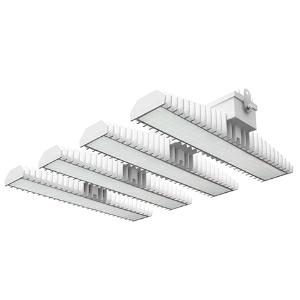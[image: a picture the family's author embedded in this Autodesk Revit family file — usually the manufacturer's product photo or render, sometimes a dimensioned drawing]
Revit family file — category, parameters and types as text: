
# Revit family: 3f_filippi_-_3f_lem_ht_concentrato_3f_filippi_-_59034_a0812_-_3f_lem_4_ht_led_120_cr_conc___vs_332a
name_source: partatom
category: Lighting Fixtures
units: mm (PartAtom-declared; Revit-internal decimal feet)

## family parameters
Cut with Voids When Loaded = No
Host = Face
Light Source = No
Part Type = Normal
Room Calculation Point = No
Round Connector Dimension = Use Diameter
Shared = No

## types (1)
- 3F Filippi - 3F LEM HT Concentrato (1 x LED, 16911 lm, 136 W, 4000 K)
    Apparent Load = 136 VA
    Approval mark = ENEC
    CIE Flux Codes = 78 93 98 100 100
    Color Rendering = 80
    Color Temperature = 4000 K
    Control Gear = Electronic ballast
    Default Elevation = 1800 mm
    Description = Industrial luminaire with high light output and high luminous efficiency designed with the most innovative technologies for environments with temperature up to 70°C.

ILLUMINOTECHNICAL
Luminous efficiency 100% (DLOR 98%, ULOR 2%).
Initial luminous flux of the luminaire 16911 lm.
Direct symmetric narrow distribution: the illuminated area has a elliptical shape.
Installation Interdistance Transv.D = 0.60 x hu - Long.D = 0.91 x hu.
Tabular UGR (CIE 117 - 4H-8H; S=0.25H; 70/50/20): RUG 18.7 - 20.2.
Beam angle: 38° - 61°.
Luminous efficacy 124 lm/W.
Lifetime (L93/B10): 30000 h. (tq+25°C)
Lifetime (L90/B10): 50000 h. (tq+25°C)
Lifetime (L85/B10): 80000 h. (tq+25°C)
Lifetime (L80/B10): 100000 h. (tq+25°C)
Lifetime (L85/B10): 50000 h. (tq+70°C)
Sudden decreased luminous flux after 50000 hours: 0% (C0).
Photobiological safety in compliance with IEC/TR 62778: RG0 risk exempt, (IEC 62471).
In compliance with IEC/EN 62722-2-1 - IEC/EN 62717 standards.
Luminous flux at +70°C: -13.5%.

SOURCE
4 Mid-Power linear LED modules 30W/840.
Energy efficiency class (UE 2019/2020 - UE 2019/2015): C.
CIE 13.3 Colour rendering index: CRI >80 (R9 <50%).
IES TM-30 Fidelity Index: Rf = 84 Rg = 95.
CCT nominal colour temperature 4000 K.
Colour initial tolerance (MacAdam): SDCM 3.

MECHANICAL
Passive modular heatsinks in die-casted aluminium, painted in white colour.
To optimize the thermal management of the LED module, the heatsinks are oversized and provided with self-cleaning of cooling fins.
Wiring body in aluminium and galvanised steel anchored solidly to the sinks and thermally separated.
3F Lens lenses with high luminous efficiency, transparent polycarbonate, fixed to the LED modules.
Fixing brackets in stainless steel.
Luminaire with limited surface temperature. - D - (EN 60598-2-24)
Dimensions: 757x542 mm, height 133 mm. Weight 18.14 kg.
IP65 protection degree.
Mechanical strength to impacts IK08 (5 joule).
Glow-wire test resistance 850°C.

ELECTRICAL
Halogen Free electronic wiring 230V-50/60Hz, power factor 0.97, THD <25%, constant output current, class I, 2 driver.
Power of the luminaire 136 W.
CE - IEC 60598-1 - EN 60598-1.
SAFE FLICKER: PstLM=<1 and SVM=<0.4 (IEC TR 61547-1 and IEC TR 63158), to ensure a more comfortable and safe light.
Luminaire compliant with EN 60598-2-22 for power supply from a centralised emergency system CPSS (Central Power Supply System), not incorporated in the luminaire - high risk areas excluded. The default power and flux are 100% in AC and 100% in DC.
Ambient temperature from -30°C to +70°C.
Temperature class T6 max 85°C.
Quick connection via M20 3P connector with 9-13 mm tightening range.
Power unit positioned on a separate compartment by the LED module to ensure optimum temperatures of cabling components, to be inspectable and maintainable.
Relative humidity UR: <85%.

INSTALLATION
Ceiling / Suspended / Wall.
All accessories dedicated to this product are available on the Catalog and on our website www.3F-Filippi.com.

ACCESSORIES
A0812 - Anti-glare microprismatic VS moulded glass, tempered, not flammable, with sealing gasket.
One required for each light module. The pack contains 10 pieces.

APPLICATIONS
In commercial environments, exhibition and industrial areas, stores, open areas.
Applications with high ambient temperature up to 70°C.

WARNING
Fixture not suitable for cold stores with an ambient temperature <0°C and/or relative humidity >85%.
Luminaire designed for disposal/recycling at end-of-life.
Replaceable (LED only) light source by a professional. Replaceable control gear by a professional.
    Height = 133 mm  [stored 0.436352 ft]
    Lamp = 1 x LED
    Lamp Light Flux = 16911 lm
    Lamp Power = 136 W
    Lamp count = 1
    Length = 757 mm
    Lifetime = 50000 h
    Luminous efficacy = 124 lm/W
    Manufacturer = 3F Filippi
    ModVariant = No
    Model = 3F Filippi - 59034+A0812 - 3F LEM 4 HT LED 120 CR CONC + VS
    Mounting Place = Ceiling
    Mounting Type = Pendant
    Number of Poles = 1
    OnlyDefault = Yes
    Power Factor = 1
    Product Name = 3F Filippi - 3F LEM HT Concentrato
    Product group = pendant luminaire
    ProductGroupID = 9
    Protection Class = Protection class I
    Protection Degree = IP 65
    RLX_Detail_Level = 1
    RLX_Emergency_Light_Flux = 0 lm
    RLX_Emergency_Type = 0
    RLX_Emergency_Type_DB = No
    RlxData = <blob elided: 119929 chars, md5=2f6cf99c>
    Socket = socket
    Standby Power = 0 W
    System Light Flux = 16911 lm
    System Power = 136 W
    Type Comments = Product without accessories
    Type Image = 3f_filippi_-_lem_4__a0812.jpg
    URL = http://relux.com
    VarID = ---
    Voltage = 0 V
    Weight = 0.00 kg
    Width = 542 mm

note: [stored X ft] marks values corroborated as IEEE doubles in the binary element streams (Revit-internal decimal feet)

## geometry (parser evidence)
native form markers: Blend x4, Sweep x13
no freeform markers — native parametric forms only
